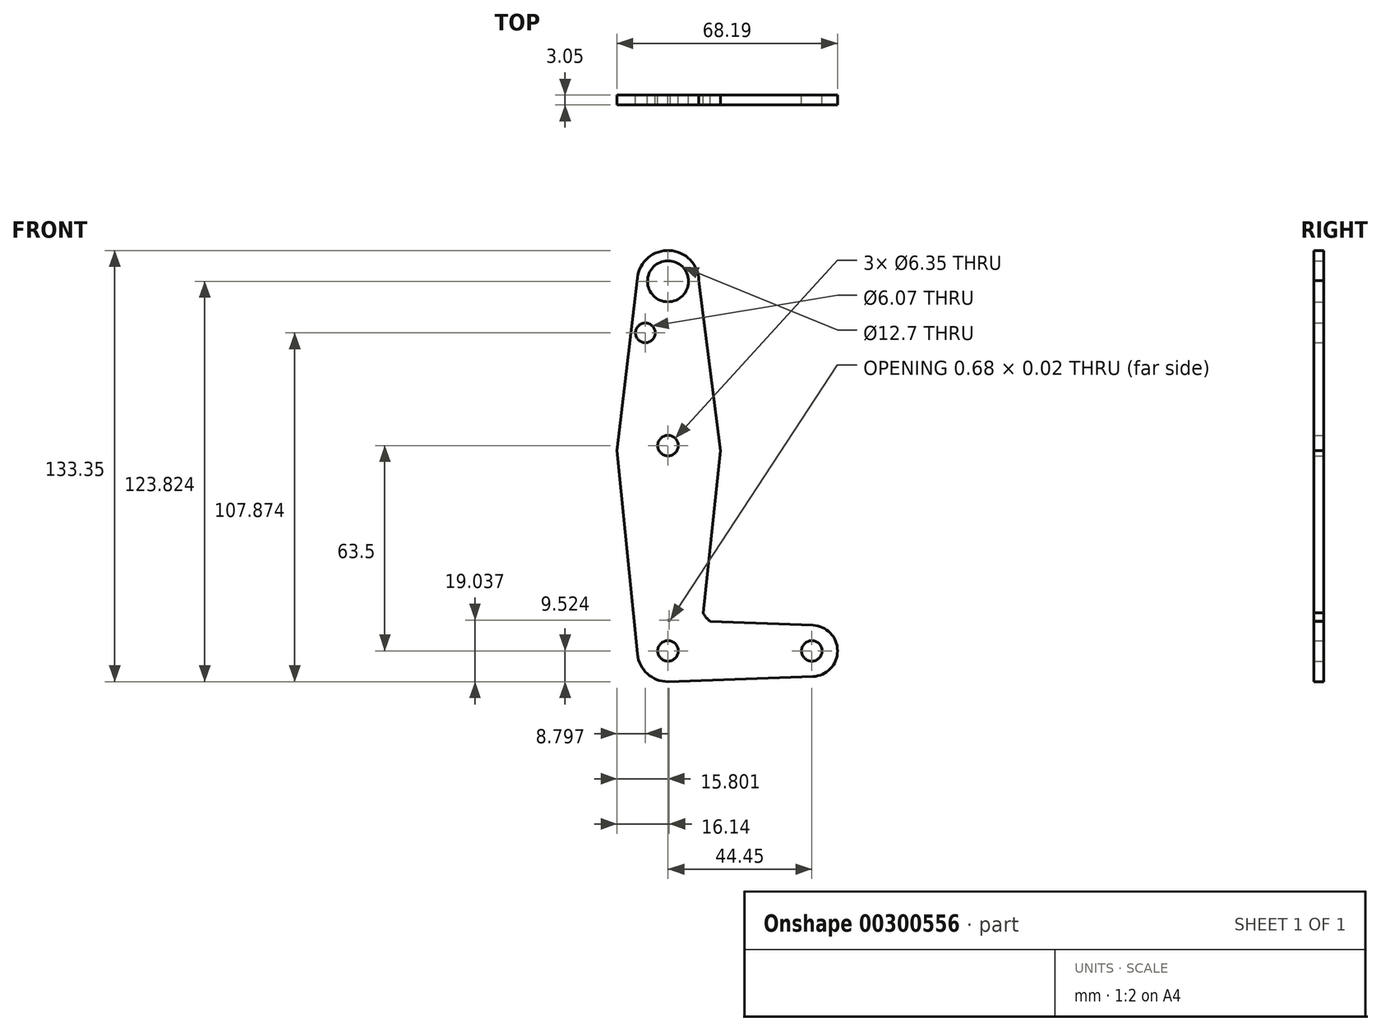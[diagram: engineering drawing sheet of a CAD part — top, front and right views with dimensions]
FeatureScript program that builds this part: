
annotation { "Feature Type Name" : "Feature", "Feature Type Description" : "" }
export const myFeature = defineFeature(function(context is Context, id is Id, definition is map)
    precondition{}
    {
        {
            var Q0;
            Q0=qCreatedBy(makeId("Front.planeOp"),FACE);
            var sketch = newSketch(context, id + "F0", { "sketchPlane" : qUnion([Q0])});
            skLineSegment(sketch, "E0", {"start": v(-45.75, 84.5) * mm, "end": v(-45.75, 33.7) * mm});
            skLineSegment(sketch, "E1", {"start": v(-45.75, 33.7) * mm, "end": v(-45.75, -29.8) * mm});
            skLineSegment(sketch, "E2", {"start": v(-45.75, -29.8) * mm, "end": v(-1.3, -29.8) * mm});
            skCircle(sketch, "E3", {"center": v(-45.75, 84.5) * mm, "radius": 9.53 * mm});
            skCircle(sketch, "E4", {"center": v(-45.75, 33.7) * mm, "radius": 15.88 * mm});
            skCircle(sketch, "E5", {"center": v(-45.75, -29.8) * mm, "radius": 9.53 * mm});
            skCircle(sketch, "E6", {"center": v(-1.3, -29.8) * mm, "radius": 7.94 * mm});
            skLineSegment(sketch, "E7", {"start": v(-55.2, 85.65) * mm, "end": v(-61.55, 32.12) * mm});
            skLineSegment(sketch, "E8", {"start": v(-36.23, 84.69) * mm, "end": v(-29.55, 32.12) * mm});
            skLineSegment(sketch, "E9", {"start": v(-61.55, 32.12) * mm, "end": v(-55.23, -30.76) * mm});
            skLineSegment(sketch, "E10", {"start": v(-29.55, 32.12) * mm, "end": v(-36.17, -29.8) * mm});
            skLineSegment(sketch, "E11", {"start": v(-45.75, -20.28) * mm, "end": v(-1.02, -21.87) * mm});
            skLineSegment(sketch, "E12", {"start": v(-45.75, -39.33) * mm, "end": v(-1.02, -37.74) * mm});
            skArc(sketch, "E13", {"start": v(-34, -9.5) * mm, "mid": v(-33.65, -19.83) * mm, "end": v(-23.38, -21.08) * mm});
            skCircle(sketch, "E14", {"center": v(-45.75, 33.7) * mm, "radius": 3.18 * mm});
            skCircle(sketch, "E15", {"center": v(-45.75, 84.5) * mm, "radius": 6.35 * mm});
            skCircle(sketch, "E16", {"center": v(-45.75, -29.8) * mm, "radius": 3.18 * mm});
            skCircle(sketch, "E17", {"center": v(-1.3, -29.8) * mm, "radius": 3.18 * mm});
            skCircle(sketch, "E18", {"center": v(-52.75, 68.54) * mm, "radius": 3.04 * mm});
            skSolve(sketch);
        }
        {
            var Q0;
            Q0=makeQuery(id+"F0.imprint","IMPRINT",FACE,{"disambiguationData":[TD([[makeQuery(id+"F0.imprint","IMPRINT",EDGE,{"derivedFrom":sQuery(id+"F0.wireOp",EDGE,"E18")}),-1.0]])]});
            var Q1;
            {var subQ0=sQuery(id+"F0.wireOp",EDGE,"E3");var subQ1=sQuery(id+"F0.wireOp",EDGE,"E0");var subQ2=makeQuery(id+"F0.imprint","INTERSECT",VERTEX,{"derivedFrom":[subQ1,subQ0]});Q1=makeQuery(id+"F0.imprint","IMPRINT",FACE,{"disambiguationData":[TD([[makeQuery(id+"F0.imprint","IMPRINT",EDGE,{"disambiguationData":[TD([[subQ2,-1.0]])],"derivedFrom":subQ1}),1.0]])]});}
            var Q2;
            Q2=makeQuery(id+"F0.imprint","IMPRINT",FACE,{"disambiguationData":[TD([[makeQuery(id+"F0.imprint","IMPRINT",EDGE,{"derivedFrom":sQuery(id+"F0.wireOp",EDGE,"E15")}),-1.0]])]});
            var Q3;
            {var subQ1=sQuery(id+"F0.wireOp",EDGE,"E4");var subQ3=sQuery(id+"F0.wireOp",EDGE,"E0");var subQ4=makeQuery(id+"F0.imprint","INTERSECT",VERTEX,{"derivedFrom":[subQ3,subQ1]});Q3=makeQuery(id+"F0.imprint","IMPRINT",FACE,{"disambiguationData":[TD([[makeQuery(id+"F0.imprint","IMPRINT",EDGE,{"disambiguationData":[TD([[subQ4,-1.0]])],"derivedFrom":subQ3}),-1.0]])]});}
            var Q4;
            {var subQ3=sQuery(id+"F0.wireOp",EDGE,"E4");var subQ6=sQuery(id+"F0.wireOp",EDGE,"E0");var subQ7=makeQuery(id+"F0.imprint","INTERSECT",VERTEX,{"derivedFrom":[subQ6,subQ3]});Q4=makeQuery(id+"F0.imprint","IMPRINT",FACE,{"disambiguationData":[TD([[makeQuery(id+"F0.imprint","IMPRINT",EDGE,{"disambiguationData":[TD([[subQ7,-1.0]])],"derivedFrom":subQ6}),1.0]])]});}
            var Q5;
            {var subQ5=sQuery(id+"F0.wireOp",EDGE,"E8");var subQ6=sQuery(id+"F0.wireOp",EDGE,"E4");var subQ7=makeQuery(id+"F0.imprint","INTERSECT",VERTEX,{"derivedFrom":[subQ6,subQ5]});Q5=makeQuery(id+"F0.imprint","IMPRINT",FACE,{"disambiguationData":[TD([[makeQuery(id+"F0.imprint","IMPRINT",EDGE,{"disambiguationData":[TD([[subQ7,1.0]])],"derivedFrom":subQ6}),-1.0]])]});}
            var Q6;
            {var subQ5=sQuery(id+"F0.wireOp",EDGE,"E9");Q6=makeQuery(id+"F0.imprint","IMPRINT",FACE,{"disambiguationData":[TD([[makeQuery(id+"F0.imprint","IMPRINT",EDGE,{"derivedFrom":subQ5}),1.0]])]});}
            var Q7;
            {var subQ3=sQuery(id+"F0.wireOp",EDGE,"E2");var subQ8=makeQuery(id+"F0.imprint","INTERSECT",VERTEX,{"derivedFrom":[subQ3,sQuery(id+"F0.wireOp",EDGE,"E10")]});Q7=makeQuery(id+"F0.imprint","IMPRINT",FACE,{"disambiguationData":[TD([[makeQuery(id+"F0.imprint","IMPRINT",EDGE,{"disambiguationData":[TD([[subQ8,1.0]])],"derivedFrom":subQ3}),-1.0]])]});}
            var Q8;
            {var subQ0=sQuery(id+"F0.wireOp",EDGE,"E10");var subQ1=sQuery(id+"F0.wireOp",EDGE,"E2");var subQ2=makeQuery(id+"F0.imprint","INTERSECT",VERTEX,{"derivedFrom":[subQ1,subQ0]});Q8=makeQuery(id+"F0.imprint","IMPRINT",FACE,{"disambiguationData":[TD([[makeQuery(id+"F0.imprint","IMPRINT",EDGE,{"disambiguationData":[TD([[subQ2,-1.0]])],"derivedFrom":subQ1}),1.0]])]});}
            var Q9;
            {var subQ0=sQuery(id+"F0.wireOp",EDGE,"E10");var subQ1=sQuery(id+"F0.wireOp",EDGE,"E2");var subQ2=makeQuery(id+"F0.imprint","INTERSECT",VERTEX,{"derivedFrom":[subQ1,subQ0]});Q9=makeQuery(id+"F0.imprint","IMPRINT",FACE,{"disambiguationData":[TD([[makeQuery(id+"F0.imprint","IMPRINT",EDGE,{"disambiguationData":[TD([[subQ2,1.0]])],"derivedFrom":subQ1}),1.0]])]});}
            var Q10;
            {var subQ1=sQuery(id+"F0.wireOp",EDGE,"E2");var subQ5=sQuery(id+"F0.wireOp",EDGE,"E16");var subQ6=makeQuery(id+"F0.imprint","INTERSECT",VERTEX,{"derivedFrom":[subQ1,subQ5]});Q10=makeQuery(id+"F0.imprint","IMPRINT",FACE,{"disambiguationData":[TD([[makeQuery(id+"F0.imprint","IMPRINT",EDGE,{"disambiguationData":[TD([[subQ6,-1.0]])],"derivedFrom":subQ1}),1.0]])]});}
            var Q11;
            {var subQ7=sQuery(id+"F0.wireOp",EDGE,"E16");var subQ8=sQuery(id+"F0.wireOp",EDGE,"E2");var subQ9=makeQuery(id+"F0.imprint","INTERSECT",VERTEX,{"derivedFrom":[subQ8,subQ7]});Q11=makeQuery(id+"F0.imprint","IMPRINT",FACE,{"disambiguationData":[TD([[makeQuery(id+"F0.imprint","IMPRINT",EDGE,{"disambiguationData":[TD([[subQ9,-1.0]])],"derivedFrom":subQ8}),-1.0]])]});}
            var Q12;
            Q12=makeQuery(id+"F0.imprint","IMPRINT",FACE,{"disambiguationData":[TD([[makeQuery(id+"F0.imprint","IMPRINT",EDGE,{"derivedFrom":sQuery(id+"F0.wireOp",EDGE,"E17")}),-1.0]])]});
            var Q13;
            {var subQ0=sQuery(id+"F0.wireOp",EDGE,"E13");var subQ1=sQuery(id+"F0.wireOp",EDGE,"E10");var subQ2=makeQuery(id+"F0.imprint","INTERSECT",VERTEX,{"disambiguationData":[OD(1.0)],"derivedFrom":[subQ1,subQ0]});Q13=makeQuery(id+"F0.imprint","IMPRINT",FACE,{"disambiguationData":[TD([[makeQuery(id+"F0.imprint","IMPRINT",EDGE,{"disambiguationData":[TD([[subQ2,-1.0]])],"derivedFrom":subQ1}),1.0]])]});}
            var Q14;
            {var subQ0=sQuery(id+"F0.wireOp",EDGE,"E13");var subQ1=sQuery(id+"F0.wireOp",EDGE,"E10");var subQ2=makeQuery(id+"F0.imprint","INTERSECT",VERTEX,{"disambiguationData":[OD(0.0)],"derivedFrom":[subQ1,subQ0]});Q14=makeQuery(id+"F0.imprint","IMPRINT",FACE,{"disambiguationData":[TD([[makeQuery(id+"F0.imprint","IMPRINT",EDGE,{"disambiguationData":[TD([[subQ2,-1.0]])],"derivedFrom":subQ1}),-1.0]])]});}
            var Q15;
            {var subQ0=sQuery(id+"F0.wireOp",EDGE,"E13");var subQ1=sQuery(id+"F0.wireOp",EDGE,"E11");var subQ2=makeQuery(id+"F0.imprint","INTERSECT",VERTEX,{"disambiguationData":[OD(0.0)],"derivedFrom":[subQ1,subQ0]});Q15=makeQuery(id+"F0.imprint","IMPRINT",FACE,{"disambiguationData":[TD([[makeQuery(id+"F0.imprint","IMPRINT",EDGE,{"disambiguationData":[TD([[subQ2,1.0]])],"derivedFrom":subQ1}),-1.0]])]});}
            extrude(context, id + "F1", {"entities" : qUnion([Q0, Q1, Q2, Q3, Q4, Q5, Q6, Q7, Q8, Q9, Q10, Q11, Q12, Q13, Q14, Q15]), "depth" : 3.05 * mm});
        }
    });
